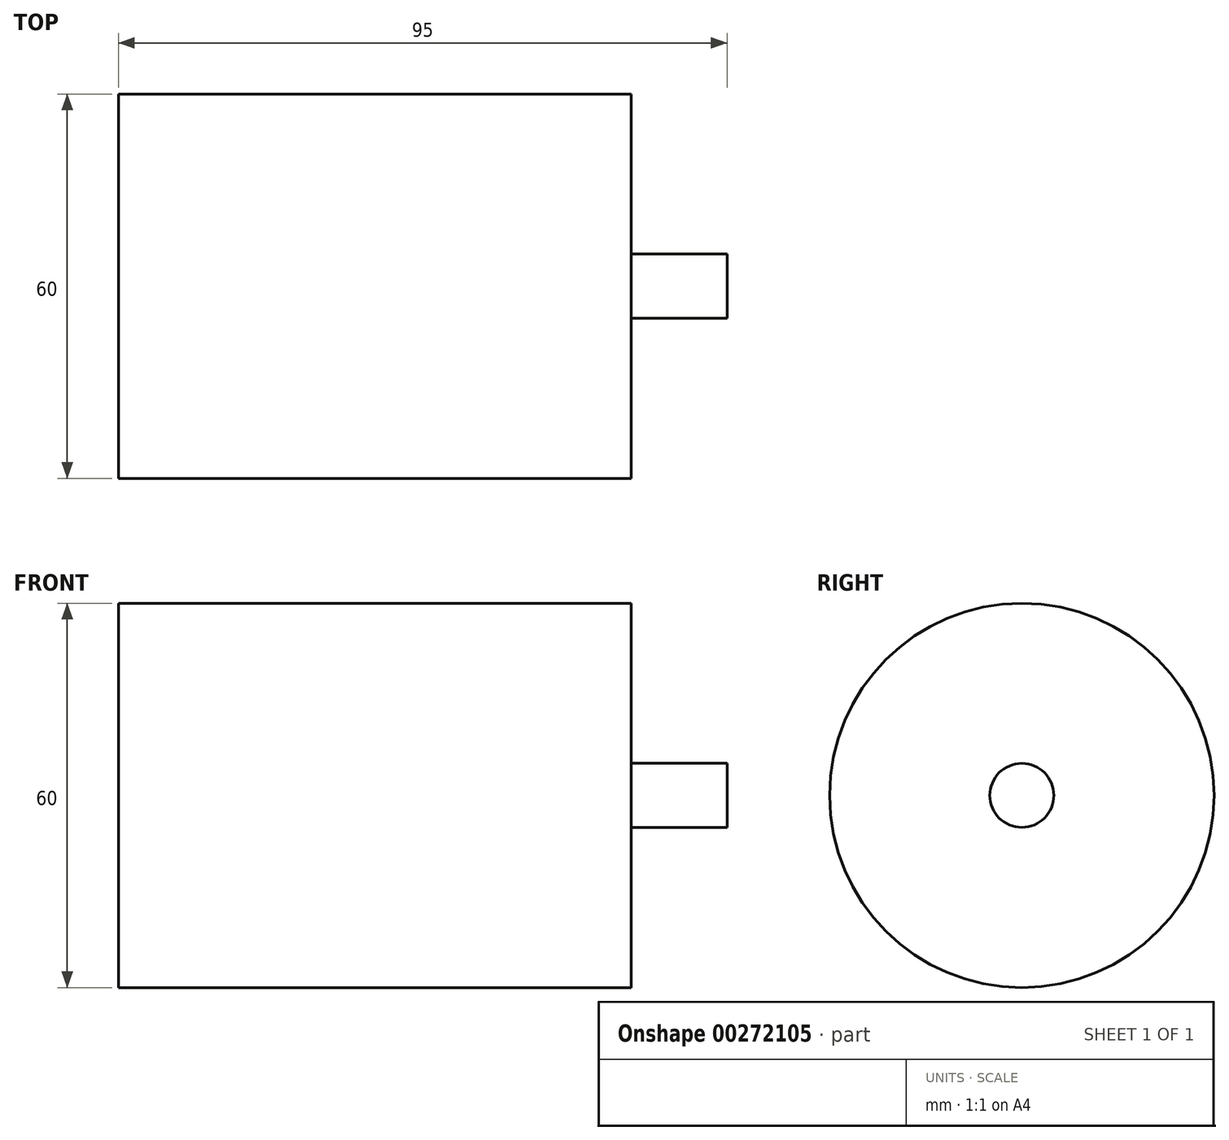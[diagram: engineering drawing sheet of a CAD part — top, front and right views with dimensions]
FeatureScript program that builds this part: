
annotation { "Feature Type Name" : "Feature", "Feature Type Description" : "" }
export const myFeature = defineFeature(function(context is Context, id is Id, definition is map)
    precondition{}
    {
        {
            var Q0;
            Q0=qCreatedBy(makeId("Front.planeOp"),FACE);
            var sketch = newSketch(context, id + "F0", { "sketchPlane" : qUnion([Q0])});
            skLineSegment(sketch, "E0", {"start": v(-119.51, 0) * mm, "end": v(134.65, 0) * mm, "construction": true});
            skLineSegment(sketch, "E1", {"start": v(0, 0) * mm, "end": v(0, 30) * mm});
            skLineSegment(sketch, "E2", {"start": v(0, 30) * mm, "end": v(80, 30) * mm});
            skLineSegment(sketch, "E3", {"start": v(80, 30) * mm, "end": v(80, 5) * mm});
            skLineSegment(sketch, "E4", {"start": v(80, 5) * mm, "end": v(95, 5) * mm});
            skLineSegment(sketch, "E5", {"start": v(95, 5) * mm, "end": v(95, 0) * mm});
            skLineSegment(sketch, "E6", {"start": v(0, 0) * mm, "end": v(95, 0) * mm});
            skSolve(sketch);
        }
        {
            var Q0;
            Q0 = qSketchRegion(id + "F0", true);
            var Q1;
            Q1=sQuery(id+"F0.wireOp",EDGE,"E0");
            revolve(context, id + "F1", {"entities" : qUnion([Q0]), "axis" : qUnion([Q1]), "revolveType" : RevolveType.FULL});
        }
    });
